# Revit family: RN 90025 Optifitt-Serra-Nippel doppio
name_source: partatom
category: Rohrformteile
units: mm (PartAtom-declared; Revit-internal decimal feet)

## family parameters
Arbeitsebenenbasiert = Nein
Beim Laden mit Abzugskörper schneiden = Nein
Bemaßung runder Anschluss = Durchmesser verwenden
Gemeinsam genutzt = Nein
Immer vertikal = Ja
Teiletyp = Nicht definiert

## types (9) — shared parameters
1.010.00.2 Blattnummer der Richtlinie = 29
1.010.00.3 Ausgabedatum (Monat) der Richtlinie = 201308
1.010.00.4 Herstellername = R. Nussbaum AG
1.010.00.5 Revisionsdatum der Datei = 20190521
1.010.00.6 Webadresse des Herstellers = http://www.nussbaum.ch
1.100.00.4 Produktbezeichnung = Versorgung
1.110.00.2 Index = 3
1.110.00.4 Produktbezeichnung = Optifitt-Serra
1.960/3L.00.8 Link (URL) = https://www.nussbaum.ch
29.700.00.4 Produktname = Optifitt-Serra-Doppelnippel
29.700.00.5 Produktkennung = 2
29.700.00.6 Querschnittsform = 1
29.700.00.7 Nennweitensystem = DN
29.700.00.8 Nenndrucksystem = PN
29.710.02.4 Nenndruck = 16
29.710.02.5 max. zul. Überdruck [hPa] = 1600
29.710.02.7 max. zul. Dauer-Betriebsdruck [hPa] = 1600
29.710.02.9 max. zul. Dauer-Betriebstemperatur [°C] = 90
Connector Visibility = Nein
EnclosingSpace Visibility = Nein
Hersteller = R. Nussbaum AG
URL = https://www.nussbaum.ch

## per-type parameters (varying)
- DN=65: 1.800.00.3 TGA-Nummer=01900300000000000000000000000000000000000000000015000000000000000020; 1.800.00.4 Kommentarfeld=90025.10, Optifitt-Serra-Doppelnippel, DN=65, L=78, R=2½; 1.810.00.3 Hersteller-Bestellnummer=90025.1; 1.810.00.4 DATANORM-Nummer=90025.1; 1.810.00.5 StLB-Nummer=214.318; 1.810.00.6 GTIN-Nummer=7612945033734; 29.710.02.10 Formstück-Gewicht [kg]=0.868; 29.710.02.3 Benennung=Optifitt-Serra-Doppelnippel, DN=65, L=78, R=2½; CONNECTOR0_DIAMETER_dX_0r=65 mm; CONNECTOR0_dX_01=27 mm; CONNECTOR0_ref_dX=27 mm; CONNECTOR1_DIAMETER_dX_0r=65 mm; CONNECTOR1_dX_00=51 mm; CONNECTOR1_dX_01=78 mm; CONNECTOR1_ref_dX=51 mm; CONNECTOR1_ref_dX2=78 mm; Modell=90025.1; R. Nussbaum AG 90025.02 de Visibility=Nein; R. Nussbaum AG 90025.03 de Visibility=Nein; R. Nussbaum AG 90025.04 de Visibility=Nein; R. Nussbaum AG 90025.05 de Visibility=Nein; R. Nussbaum AG 90025.06 de Visibility=Nein; R. Nussbaum AG 90025.07 de Visibility=Nein; R. Nussbaum AG 90025.08 de Visibility=Nein; R. Nussbaum AG 90025.09 de Visibility=Nein; R. Nussbaum AG 90025.10 de Visibility=Ja; Typenkommentare=Optifitt-Serra-Nippel doppio DN=65
- DN=50: 1.800.00.3 TGA-Nummer=01900300000000000000000000000000000000000000000015000000000000000008; 1.800.00.4 Kommentarfeld=90025.09, Optifitt-Serra-Doppelnippel, DN=50, L=65, R=2; 1.810.00.3 Hersteller-Bestellnummer=90025.09; 1.810.00.4 DATANORM-Nummer=90025.09; 1.810.00.5 StLB-Nummer=214.317; 1.810.00.6 GTIN-Nummer=7612945033727; 29.710.02.10 Formstück-Gewicht [kg]=0.471; 29.710.02.3 Benennung=Optifitt-Serra-Doppelnippel, DN=50, L=65, R=2; CONNECTOR0_DIAMETER_dX_0r=50 mm; CONNECTOR0_dX_01=24 mm  [stored 0.0787402 ft]; CONNECTOR0_ref_dX=24 mm  [stored 0.0787402 ft]; CONNECTOR1_DIAMETER_dX_0r=50 mm; CONNECTOR1_dX_00=41 mm  [stored 0.134514 ft]; CONNECTOR1_dX_01=65 mm; CONNECTOR1_ref_dX=41 mm  [stored 0.134514 ft]; CONNECTOR1_ref_dX2=65 mm; Modell=90025.09; R. Nussbaum AG 90025.02 de Visibility=Nein; R. Nussbaum AG 90025.03 de Visibility=Nein; R. Nussbaum AG 90025.04 de Visibility=Nein; R. Nussbaum AG 90025.05 de Visibility=Nein; R. Nussbaum AG 90025.06 de Visibility=Nein; R. Nussbaum AG 90025.07 de Visibility=Nein; R. Nussbaum AG 90025.08 de Visibility=Nein; R. Nussbaum AG 90025.09 de Visibility=Ja; R. Nussbaum AG 90025.10 de Visibility=Nein; Typenkommentare=Optifitt-Serra-Nippel doppio DN=50
- DN=40: 1.800.00.3 TGA-Nummer=01900300000000000000000000000000000000000000000015000000000000000007; 1.800.00.4 Kommentarfeld=90025.08, Optifitt-Serra-Doppelnippel, DN=40, L=52, R=1½; 1.810.00.3 Hersteller-Bestellnummer=90025.08; 1.810.00.4 DATANORM-Nummer=90025.08; 1.810.00.5 StLB-Nummer=214.316; 1.810.00.6 GTIN-Nummer=7612945033710; 29.710.02.10 Formstück-Gewicht [kg]=0.224; 29.710.02.3 Benennung=Optifitt-Serra-Doppelnippel, DN=40, L=52, R=1½; CONNECTOR0_DIAMETER_dX_0r=40 mm  [stored 0.131234 ft]; CONNECTOR0_dX_01=19 mm; CONNECTOR0_ref_dX=19 mm; CONNECTOR1_DIAMETER_dX_0r=40 mm  [stored 0.131234 ft]; CONNECTOR1_dX_00=33 mm; CONNECTOR1_dX_01=52 mm; CONNECTOR1_ref_dX=33 mm; CONNECTOR1_ref_dX2=52 mm; Modell=90025.08; R. Nussbaum AG 90025.02 de Visibility=Nein; R. Nussbaum AG 90025.03 de Visibility=Nein; R. Nussbaum AG 90025.04 de Visibility=Nein; R. Nussbaum AG 90025.05 de Visibility=Nein; R. Nussbaum AG 90025.06 de Visibility=Nein; R. Nussbaum AG 90025.07 de Visibility=Nein; R. Nussbaum AG 90025.08 de Visibility=Ja; R. Nussbaum AG 90025.09 de Visibility=Nein; R. Nussbaum AG 90025.10 de Visibility=Nein; Typenkommentare=Optifitt-Serra-Nippel doppio DN=40
- DN=32: 1.800.00.3 TGA-Nummer=01900300000000000000000000000000000000000000000015000000000000000006; 1.800.00.4 Kommentarfeld=90025.07, Optifitt-Serra-Doppelnippel, DN=32, L=53, R=1¼; 1.810.00.3 Hersteller-Bestellnummer=90025.07; 1.810.00.4 DATANORM-Nummer=90025.07; 1.810.00.5 StLB-Nummer=214.315; 1.810.00.6 GTIN-Nummer=7612945033703; 29.710.02.10 Formstück-Gewicht [kg]=0.199; 29.710.02.3 Benennung=Optifitt-Serra-Doppelnippel, DN=32, L=53, R=1¼; CONNECTOR0_DIAMETER_dX_0r=32 mm; CONNECTOR0_dX_01=19 mm; CONNECTOR0_ref_dX=19 mm; CONNECTOR1_DIAMETER_dX_0r=32 mm; CONNECTOR1_dX_00=34 mm; CONNECTOR1_dX_01=53 mm; CONNECTOR1_ref_dX=34 mm; CONNECTOR1_ref_dX2=53 mm; Modell=90025.07; R. Nussbaum AG 90025.02 de Visibility=Nein; R. Nussbaum AG 90025.03 de Visibility=Nein; R. Nussbaum AG 90025.04 de Visibility=Nein; R. Nussbaum AG 90025.05 de Visibility=Nein; R. Nussbaum AG 90025.06 de Visibility=Nein; R. Nussbaum AG 90025.07 de Visibility=Ja; R. Nussbaum AG 90025.08 de Visibility=Nein; R. Nussbaum AG 90025.09 de Visibility=Nein; R. Nussbaum AG 90025.10 de Visibility=Nein; Typenkommentare=Optifitt-Serra-Nippel doppio DN=32
- DN=25: 1.800.00.3 TGA-Nummer=01900300000000000000000000000000000000000000000015000000000000000005; 1.800.00.4 Kommentarfeld=90025.06, Optifitt-Serra-Doppelnippel, DN=25, L=45, R=1; 1.810.00.3 Hersteller-Bestellnummer=90025.06; 1.810.00.4 DATANORM-Nummer=90025.06; 1.810.00.5 StLB-Nummer=214.314; 1.810.00.6 GTIN-Nummer=7612945033697; 29.710.02.10 Formstück-Gewicht [kg]=0.113; 29.710.02.3 Benennung=Optifitt-Serra-Doppelnippel, DN=25, L=45, R=1; CONNECTOR0_DIAMETER_dX_0r=25 mm  [stored 0.082021 ft]; CONNECTOR0_dX_01=17 mm; CONNECTOR0_ref_dX=17 mm; CONNECTOR1_DIAMETER_dX_0r=25 mm  [stored 0.082021 ft]; CONNECTOR1_dX_00=28 mm; CONNECTOR1_dX_01=45 mm  [stored 0.147638 ft]; CONNECTOR1_ref_dX=28 mm; CONNECTOR1_ref_dX2=45 mm  [stored 0.147638 ft]; Modell=90025.06; R. Nussbaum AG 90025.02 de Visibility=Nein; R. Nussbaum AG 90025.03 de Visibility=Nein; R. Nussbaum AG 90025.04 de Visibility=Nein; R. Nussbaum AG 90025.05 de Visibility=Nein; R. Nussbaum AG 90025.06 de Visibility=Ja; R. Nussbaum AG 90025.07 de Visibility=Nein; R. Nussbaum AG 90025.08 de Visibility=Nein; R. Nussbaum AG 90025.09 de Visibility=Nein; R. Nussbaum AG 90025.10 de Visibility=Nein; Typenkommentare=Optifitt-Serra-Nippel doppio DN=25
- DN=20: 1.800.00.3 TGA-Nummer=01900300000000000000000000000000000000000000000015000000000000000004; 1.800.00.4 Kommentarfeld=90025.05, Optifitt-Serra-Doppelnippel, DN=20, L=40, R=¾; 1.810.00.3 Hersteller-Bestellnummer=90025.05; 1.810.00.4 DATANORM-Nummer=90025.05; 1.810.00.5 StLB-Nummer=214.313; 1.810.00.6 GTIN-Nummer=7612945033680; 29.710.02.10 Formstück-Gewicht [kg]=0.07; 29.710.02.3 Benennung=Optifitt-Serra-Doppelnippel, DN=20, L=40, R=¾; CONNECTOR0_DIAMETER_dX_0r=20 mm; CONNECTOR0_dX_01=15 mm; CONNECTOR0_ref_dX=15 mm; CONNECTOR1_DIAMETER_dX_0r=20 mm; CONNECTOR1_dX_00=25 mm  [stored 0.082021 ft]; CONNECTOR1_dX_01=40 mm  [stored 0.131234 ft]; CONNECTOR1_ref_dX=25 mm  [stored 0.082021 ft]; CONNECTOR1_ref_dX2=40 mm  [stored 0.131234 ft]; Modell=90025.05; R. Nussbaum AG 90025.02 de Visibility=Nein; R. Nussbaum AG 90025.03 de Visibility=Nein; R. Nussbaum AG 90025.04 de Visibility=Nein; R. Nussbaum AG 90025.05 de Visibility=Ja; R. Nussbaum AG 90025.06 de Visibility=Nein; R. Nussbaum AG 90025.07 de Visibility=Nein; R. Nussbaum AG 90025.08 de Visibility=Nein; R. Nussbaum AG 90025.09 de Visibility=Nein; R. Nussbaum AG 90025.10 de Visibility=Nein; Typenkommentare=Optifitt-Serra-Nippel doppio DN=20
- DN=15: 1.800.00.3 TGA-Nummer=01900300000000000000000000000000000000000000000015000000000000000003; 1.800.00.4 Kommentarfeld=90025.04, Optifitt-Serra-Doppelnippel, DN=15, L=37, R=½; 1.810.00.3 Hersteller-Bestellnummer=90025.04; 1.810.00.4 DATANORM-Nummer=90025.04; 1.810.00.5 StLB-Nummer=214.312; 1.810.00.6 GTIN-Nummer=7612945033673; 29.710.02.10 Formstück-Gewicht [kg]=0.045; 29.710.02.3 Benennung=Optifitt-Serra-Doppelnippel, DN=15, L=37, R=½; CONNECTOR0_DIAMETER_dX_0r=15 mm; CONNECTOR0_dX_01=13 mm; CONNECTOR0_ref_dX=13 mm; CONNECTOR1_DIAMETER_dX_0r=15 mm; CONNECTOR1_dX_00=24 mm  [stored 0.0787402 ft]; CONNECTOR1_dX_01=37 mm; CONNECTOR1_ref_dX=24 mm  [stored 0.0787402 ft]; CONNECTOR1_ref_dX2=37 mm; Modell=90025.04; R. Nussbaum AG 90025.02 de Visibility=Nein; R. Nussbaum AG 90025.03 de Visibility=Nein; R. Nussbaum AG 90025.04 de Visibility=Ja; R. Nussbaum AG 90025.05 de Visibility=Nein; R. Nussbaum AG 90025.06 de Visibility=Nein; R. Nussbaum AG 90025.07 de Visibility=Nein; R. Nussbaum AG 90025.08 de Visibility=Nein; R. Nussbaum AG 90025.09 de Visibility=Nein; R. Nussbaum AG 90025.10 de Visibility=Nein; Typenkommentare=Optifitt-Serra-Nippel doppio DN=15
- DN=1: 1.800.00.3 TGA-Nummer=01900300000000000000000000000000000000000000000015000000000000000002; 1.800.00.4 Kommentarfeld=90025.03, Optifitt-Serra-Doppelnippel, DN=10, L=29, R=3/8; 1.810.00.3 Hersteller-Bestellnummer=90025.03; 1.810.00.4 DATANORM-Nummer=90025.03; 1.810.00.5 StLB-Nummer=214.311; 1.810.00.6 GTIN-Nummer=7612945033666; 29.710.02.10 Formstück-Gewicht [kg]=0.028; 29.710.02.3 Benennung=Optifitt-Serra-Doppelnippel, DN=10, L=29, R=3/8; CONNECTOR0_DIAMETER_dX_0r=12 mm  [stored 0.0393701 ft]; CONNECTOR0_dX_01=10 mm  [stored 0.0328084 ft]; CONNECTOR0_ref_dX=10 mm  [stored 0.0328084 ft]; CONNECTOR1_DIAMETER_dX_0r=12 mm  [stored 0.0393701 ft]; CONNECTOR1_dX_00=19 mm; CONNECTOR1_dX_01=29 mm; CONNECTOR1_ref_dX=19 mm; CONNECTOR1_ref_dX2=29 mm; Modell=90025.03; R. Nussbaum AG 90025.02 de Visibility=Nein; R. Nussbaum AG 90025.03 de Visibility=Ja; R. Nussbaum AG 90025.04 de Visibility=Nein; R. Nussbaum AG 90025.05 de Visibility=Nein; R. Nussbaum AG 90025.06 de Visibility=Nein; R. Nussbaum AG 90025.07 de Visibility=Nein; R. Nussbaum AG 90025.08 de Visibility=Nein; R. Nussbaum AG 90025.09 de Visibility=Nein; R. Nussbaum AG 90025.10 de Visibility=Nein; Typenkommentare=Optifitt-Serra-Nippel doppio DN=10
- DN=10: 1.800.00.3 TGA-Nummer=01900300000000000000000000000000000000000000000015000000000000000001; 1.800.00.4 Kommentarfeld=90025.02, Optifitt-Serra-Doppelnippel, DN=10, L=20, R=¼; 1.810.00.3 Hersteller-Bestellnummer=90025.02; 1.810.00.4 DATANORM-Nummer=90025.02; 1.810.00.6 GTIN-Nummer=7612945033659; 29.710.02.10 Formstück-Gewicht [kg]=0.013; 29.710.02.3 Benennung=Optifitt-Serra-Doppelnippel, DN=10, L=20, R=¼; CONNECTOR0_DIAMETER_dX_0r=8 mm  [stored 0.0262467 ft]; CONNECTOR0_dX_01=10 mm  [stored 0.0328084 ft]; CONNECTOR0_ref_dX=10 mm  [stored 0.0328084 ft]; CONNECTOR1_DIAMETER_dX_0r=8 mm  [stored 0.0262467 ft]; CONNECTOR1_dX_00=10 mm  [stored 0.0328084 ft]; CONNECTOR1_dX_01=20 mm; CONNECTOR1_ref_dX=10 mm  [stored 0.0328084 ft]; CONNECTOR1_ref_dX2=20 mm; Modell=90025.02; R. Nussbaum AG 90025.02 de Visibility=Ja; R. Nussbaum AG 90025.03 de Visibility=Nein; R. Nussbaum AG 90025.04 de Visibility=Nein; R. Nussbaum AG 90025.05 de Visibility=Nein; R. Nussbaum AG 90025.06 de Visibility=Nein; R. Nussbaum AG 90025.07 de Visibility=Nein; R. Nussbaum AG 90025.08 de Visibility=Nein; R. Nussbaum AG 90025.09 de Visibility=Nein; R. Nussbaum AG 90025.10 de Visibility=Nein; Typenkommentare=Optifitt-Serra-Nippel doppio DN=10

note: [stored X ft] marks values corroborated as IEEE doubles in the binary element streams (Revit-internal decimal feet)

## geometry (parser evidence)
native form markers: Sweep x2
no freeform markers — native parametric forms only
